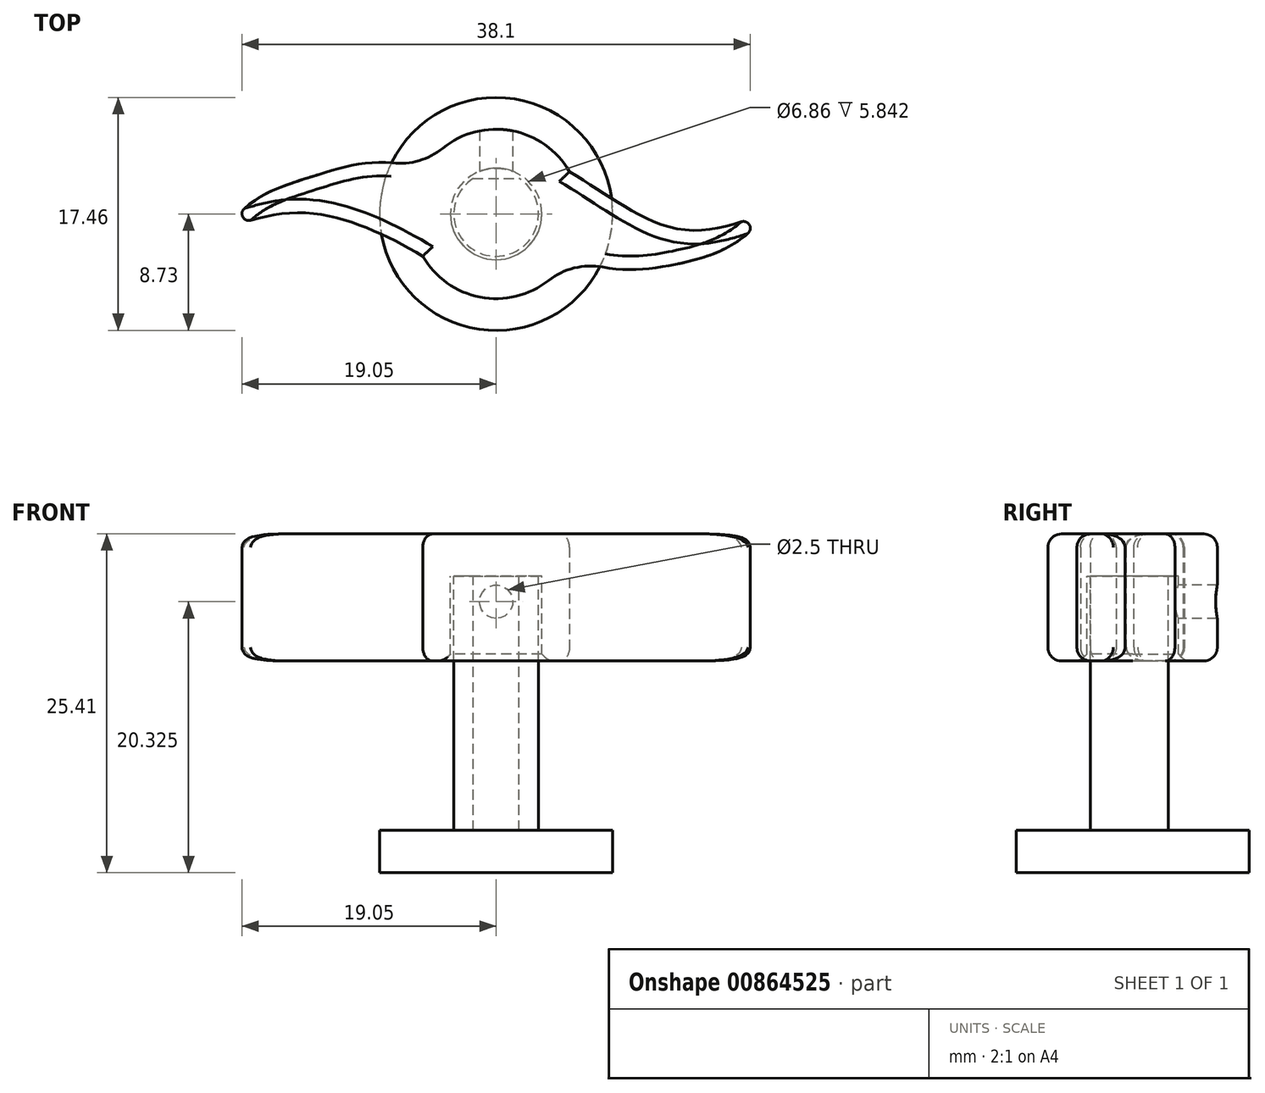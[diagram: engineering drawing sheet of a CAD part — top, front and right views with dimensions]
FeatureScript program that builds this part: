
annotation { "Feature Type Name" : "Feature", "Feature Type Description" : "" }
export const myFeature = defineFeature(function(context is Context, id is Id, definition is map)
    precondition{}
    {
        {
            var Q0;
            Q0=qCreatedBy(makeId("Top.planeOp"),FACE);
            var sketch = newSketch(context, id + "F0", { "sketchPlane" : qUnion([Q0])});
            skArc(sketch, "E0", {"start": v(-1.72, 2.67) * mm, "mid": v(0, -3.18) * mm, "end": v(1.72, 2.67) * mm});
            skLineSegment(sketch, "E1", {"start": v(-1.72, 2.67) * mm, "end": v(1.72, 2.67) * mm});
            skSolve(sketch);
        }
        {
            var Q0;
            Q0 = qSketchRegion(id + "F0", true);
            extrude(context, id + "F1", {"entities" : qUnion([Q0]), "oppositeDirection" : true, "depth" : 19.05 * mm, "offsetDistance" : 25.4 * mm});
        }
        {
            var Q0;
            Q0=makeQuery(id+"F1.opExtrude","CAP_FACE",FACE,{"disambiguationData":[OSD([sQuery(id+"F0.wireOp",EDGE,"E0")])],"isStart":false});
            var sketch = newSketch(context, id + "F2", { "sketchPlane" : qUnion([Q0])});
            skCircle(sketch, "E2", {"center": v(0, 0) * mm, "radius": 8.73 * mm});
            skSolve(sketch);
        }
        {
            var Q0;
            Q0 = qSketchRegion(id + "F2", true);
            extrude(context, id + "F3", {"entities" : qUnion([Q0]), "operationType" : NewBodyOperationType.ADD, "depth" : 3.17 * mm, "offsetDistance" : 25.4 * mm});
        }
        {
            var Q0;
            Q0=makeQuery(id+"F1.opExtrude","CAP_FACE",FACE,{"disambiguationData":[OSD([sQuery(id+"F0.wireOp",EDGE,"E0")])],"isStart":true});
            var sketch = newSketch(context, id + "F4", { "sketchPlane" : qUnion([Q0])});
            skCircle(sketch, "E3.0", {"center": v(0, 0) * mm, "radius": 3.43 * mm});
            skArc(sketch, "E4", {"start": v(-5.5, -3.17) * mm, "mid": v(0, -6.35) * mm, "end": v(5.5, -3.17) * mm});
            skLineSegment(sketch, "E5", {"start": v(0, 0) * mm, "end": v(20.14, 0) * mm, "construction": true});
            skFitSpline(sketch, "E6", {"points": [v(5.5, -3.17) * mm, v(13.82, -3.7) * mm, v(20.14, 0) * mm], "startDerivative": vector(16.7, -8) * mm, "endDerivative": vector(9.9, 14.61) * mm});
            skFitSpline(sketch, "E7", {"points": [v(20.14, 0) * mm, v(13.82, -1.16) * mm, v(5.5, 3.17) * mm], "startDerivative": vector(-11.55, -3.79) * mm, "endDerivative": vector(-14.97, 8.97) * mm});
            skArc(sketch, "E8.filletArc", {"start": v(18.88, -1.45) * mm, "mid": v(18.98, -0.82) * mm, "end": v(18.39, -0.58) * mm});
            skFitSpline(sketch, "E9", {"points": [v(-5.5, 3.18) * mm, v(-14.03, 2.73) * mm, v(-20.01, -0.91) * mm], "startDerivative": vector(-16.7, 8.01) * mm, "endDerivative": vector(-10.02, -14.5) * mm});
            skFitSpline(sketch, "E10", {"points": [v(-20.03, -0.98) * mm, v(-14.03, 0.07) * mm, v(-5.5, -3.18) * mm], "startDerivative": vector(11.54, 3.84) * mm, "endDerivative": vector(15, -8.95) * mm});
            skArc(sketch, "E11.filletArc", {"start": v(-18.89, 0.39) * mm, "mid": v(-18.99, -0.23) * mm, "end": v(-18.4, -0.47) * mm});
            skArc(sketch, "E12.trimOffspring", {"start": v(5.5, 3.18) * mm, "mid": v(0, 6.35) * mm, "end": v(-5.5, 3.17) * mm});
            skSolve(sketch);
        }
        {
            var Q0;
            Q0=makeQuery(id+"F4.imprint","IMPRINT",FACE,{"disambiguationData":[TD([[makeQuery(id+"F4.imprint","IMPRINT",EDGE,{"derivedFrom":makeQuery(id+"F1.opExtrude","CAP_EDGE",EDGE,{"disambiguationData":[OSD([sQuery(id+"F0.wireOp",EDGE,"E0")])],"isStart":true})}),1.0]])]});
            var Q1;
            Q1=makeQuery(id+"F4.imprint","IMPRINT",FACE,{"disambiguationData":[TD([[makeQuery(id+"F4.imprint","IMPRINT",EDGE,{"derivedFrom":sQuery(id+"F4.wireOp",EDGE,"E3.0")}),1.0]])]});
            var Q2;
            Q2=makeQuery(id+"F4.imprint","IMPRINT",FACE,{"disambiguationData":[TD([[makeQuery(id+"F4.imprint","IMPRINT",EDGE,{"derivedFrom":sQuery(id+"F4.wireOp",EDGE,"E3.0")}),-1.0]])]});
            extrude(context, id + "F5", {"entities" : qUnion([Q0, Q1, Q2]), "depth" : 3.17 * mm, "offsetDistance" : 25.4 * mm});
        }
        {
            var Q0;
            Q0=makeQuery(id+"F4.imprint","IMPRINT",FACE,{"disambiguationData":[TD([[makeQuery(id+"F4.imprint","IMPRINT",EDGE,{"derivedFrom":sQuery(id+"F4.wireOp",EDGE,"E3.0")}),-1.0]])]});
            extrude(context, id + "F6", {"entities" : qUnion([Q0]), "operationType" : NewBodyOperationType.ADD, "oppositeDirection" : true, "depth" : 6.35 * mm, "offsetDistance" : 25.4 * mm});
        }
        {
            var Q0;
            {var subQ0=sQuery(id+"F4.wireOp",EDGE,"E6");var subQ1=sQuery(id+"F4.wireOp",EDGE,"E4");Q0=makeQuery(id+"F6.boolean.opBoolean","MERGE",EDGE,{"derivedFrom":[makeQuery(id+"F5.opExtrude","SWEPT_EDGE",EDGE,{"disambiguationData":[OSD([subQ1,subQ0])]}),makeQuery(id+"F6.opExtrude","SWEPT_EDGE",EDGE,{"disambiguationData":[OSD([subQ1,subQ0])]})]});}
            var Q1;
            {var subQ0=sQuery(id+"F4.wireOp",EDGE,"E12.trimOffspring");var subQ1=sQuery(id+"F4.wireOp",EDGE,"E9");Q1=makeQuery(id+"F6.boolean.opBoolean","MERGE",EDGE,{"derivedFrom":[makeQuery(id+"F5.opExtrude","SWEPT_EDGE",EDGE,{"disambiguationData":[OSD([subQ1,subQ0])]}),makeQuery(id+"F6.opExtrude","SWEPT_EDGE",EDGE,{"disambiguationData":[OSD([subQ1,subQ0])]})]});}
            fillet(context, id + "F7", {"entities" : qUnion([Q0, Q1]), "radius" : 5.08 * mm, "tangentPropagation" : true, "allowEdgeOverflow" : false});
        }
        {
            var Q0;
            Q0=makeQuery(id+"F6.opExtrude","CAP_EDGE",EDGE,{"disambiguationData":[OSD([sQuery(id+"F4.wireOp",EDGE,"E3.0")])],"isStart":false});
            chamfer(context, id + "F8", {"entities" : qUnion([Q0]), "width" : 0.5 * mm, "tangentPropagation" : true});
        }
        {
            var Q0;
            Q0=makeQuery(id+"F5.opExtrude","CAP_FACE",FACE,{"disambiguationData":[OSD([sQuery(id+"F4.wireOp",EDGE,"E4"),sQuery(id+"F4.wireOp",EDGE,"E6"),sQuery(id+"F4.wireOp",EDGE,"E7"),sQuery(id+"F4.wireOp",EDGE,"E8.filletArc"),sQuery(id+"F4.wireOp",EDGE,"E9"),sQuery(id+"F4.wireOp",EDGE,"E10"),sQuery(id+"F4.wireOp",EDGE,"E11.filletArc"),sQuery(id+"F4.wireOp",EDGE,"E12.trimOffspring")])],"isStart":false});
            var Q1;
            Q1=makeQuery(id+"F6.opExtrude","CAP_FACE",FACE,{"disambiguationData":[OSD([sQuery(id+"F4.wireOp",EDGE,"E3.0"),sQuery(id+"F4.wireOp",EDGE,"E4"),sQuery(id+"F4.wireOp",EDGE,"E6"),sQuery(id+"F4.wireOp",EDGE,"E7"),sQuery(id+"F4.wireOp",EDGE,"E8.filletArc"),sQuery(id+"F4.wireOp",EDGE,"E9"),sQuery(id+"F4.wireOp",EDGE,"E10"),sQuery(id+"F4.wireOp",EDGE,"E11.filletArc"),sQuery(id+"F4.wireOp",EDGE,"E12.trimOffspring")])],"isStart":false});
            fillet(context, id + "F9", {"entities" : qUnion([Q0, Q1]), "radius" : 1.02 * mm, "tangentPropagation" : true, "allowEdgeOverflow" : false});
        }
        {
            var Q0;
            Q0=makeQuery(id+"F1.opExtrude","SWEPT_FACE",FACE,{"disambiguationData":[OSD([sQuery(id+"F0.wireOp",EDGE,"E1")])]});
            var sketch = newSketch(context, id + "F10", { "sketchPlane" : qUnion([Q0])});
            skPoint(sketch, "E13", {"position": v(0, -1.9) * mm});
            skSolve(sketch);
        }
        {
            var Q0;
            Q0=sQuery(id+"F10.wireOp",VERTEX,"E13");
            var Q1;
            Q1=makeQuery(id+"F5.opExtrude","SWEPT_BODY",BODY,{"disambiguationData":[OSD([sQuery(id+"F4.wireOp",EDGE,"E4"),sQuery(id+"F4.wireOp",EDGE,"E6"),sQuery(id+"F4.wireOp",EDGE,"E7"),sQuery(id+"F4.wireOp",EDGE,"E8.filletArc"),sQuery(id+"F4.wireOp",EDGE,"E9"),sQuery(id+"F4.wireOp",EDGE,"E10"),sQuery(id+"F4.wireOp",EDGE,"E11.filletArc"),sQuery(id+"F4.wireOp",EDGE,"E12.trimOffspring")])]});
            hole(context, id + "F11", {"style" : HoleStyle.SIMPLE, "endStyle" : HoleEndStyle.THROUGH, "oppositeDirection" : true, "standardTappedOrClearance" : lookupTablePath({ "standard" : "ISO", "engagement" : "75%", "pitch" : "0.5 mm", "size" : "M3", "type" : "Tapped" }), "standardBlindInLast" : lookupTablePath({ "standard" : "ISO", "engagement" : "75%", "pitch" : "0.5 mm", "size" : "M3", "type" : "Tapped" }), "holeDiameter" : 2.5 * mm, "majorDiameter" : 3 * mm, "showTappedDepth" : true, "isTappedThrough" : true, "tappedDepth" : 5.6 * mm, "tapClearance" : 3, "locations" : qUnion([Q0]), "scope" : qUnion([Q1])});
        }
    });
